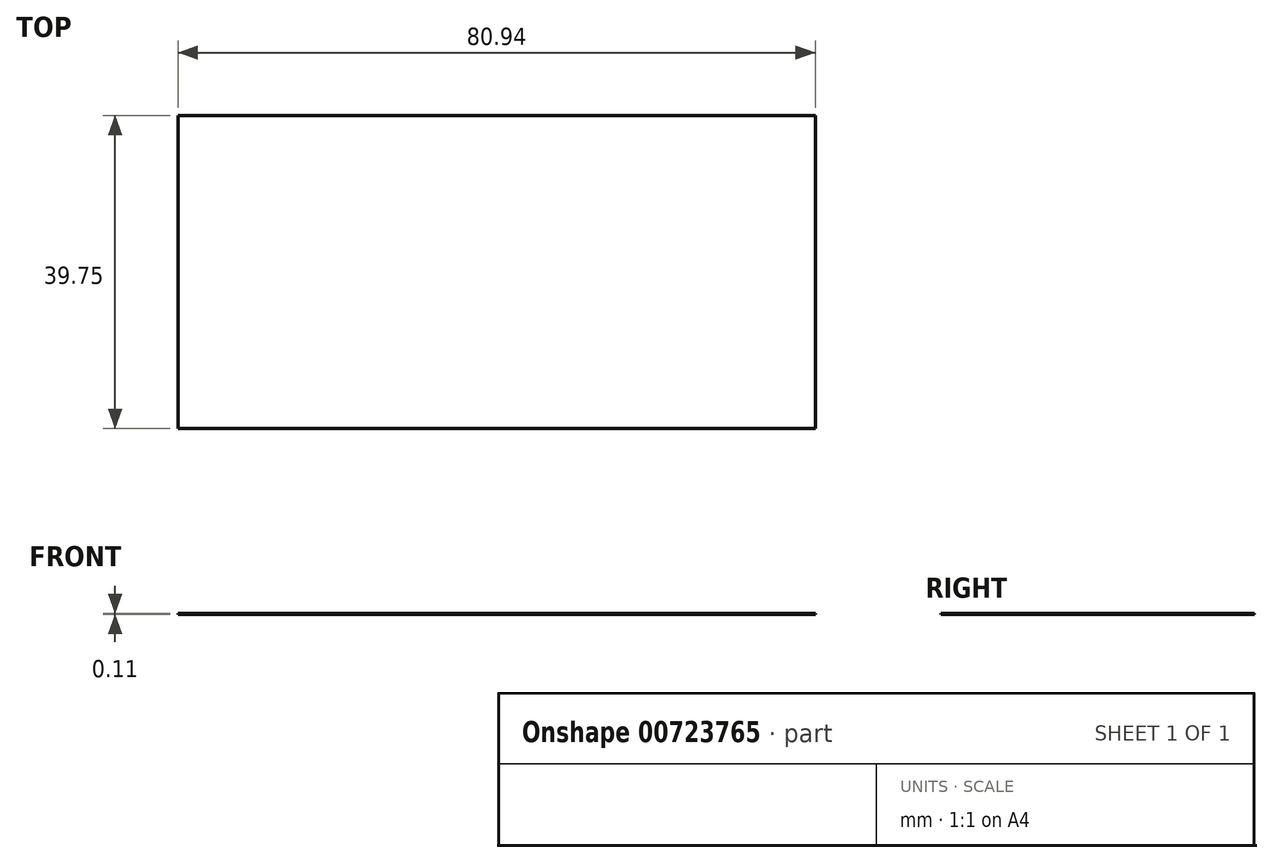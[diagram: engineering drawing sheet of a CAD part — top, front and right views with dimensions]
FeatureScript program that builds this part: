
annotation { "Feature Type Name" : "Feature", "Feature Type Description" : "" }
export const myFeature = defineFeature(function(context is Context, id is Id, definition is map)
    precondition{}
    {
        {
            var Q0;
            Q0=qCreatedBy(makeId("Top.planeOp"),FACE);
            var sketch = newSketch(context, id + "F0", { "sketchPlane" : qUnion([Q0])});
            skLineSegment(sketch, "E0.bottom", {"start": v(-24.4, 20.97) * mm, "end": v(56.54, 20.97) * mm});
            skLineSegment(sketch, "E0.top", {"start": v(-24.4, -18.78) * mm, "end": v(56.54, -18.78) * mm});
            skLineSegment(sketch, "E0.left", {"start": v(-24.4, 20.97) * mm, "end": v(-24.4, -18.78) * mm});
            skLineSegment(sketch, "E0.right", {"start": v(56.54, 20.97) * mm, "end": v(56.54, -18.78) * mm});
            skSolve(sketch);
        }
        {
            var Q0;
            Q0 = qSketchRegion(id + "F0", true);
            extrude(context, id + "F1", {"entities" : qUnion([Q0]), "depth" : .109 * mm, "offsetDistance" : 25 * mm});
        }
        {
            var Q0;
            Q0=makeQuery(id+"F1.opExtrude","SWEPT_BODY",BODY,{"disambiguationData":[OSD([sQuery(id+"F0.wireOp",EDGE,"E0.bottom"),sQuery(id+"F0.wireOp",EDGE,"E0.top"),sQuery(id+"F0.wireOp",EDGE,"E0.left"),sQuery(id+"F0.wireOp",EDGE,"E0.right")])]});
            var Q1;
            Q1=makeQuery(id+"F1.opExtrude","CAP_EDGE",EDGE,{"disambiguationData":[OSD([sQuery(id+"F0.wireOp",EDGE,"E0.top")])],"isStart":false});
            transform(context, id + "F2", {"entities" : qUnion([Q0]), "transformType" : TransformType.TRANSLATION_ENTITY, "oppositeDirectionEntity" : false, "transformLine" : qUnion([Q1]), "makeCopy" : false});
        }
    });
